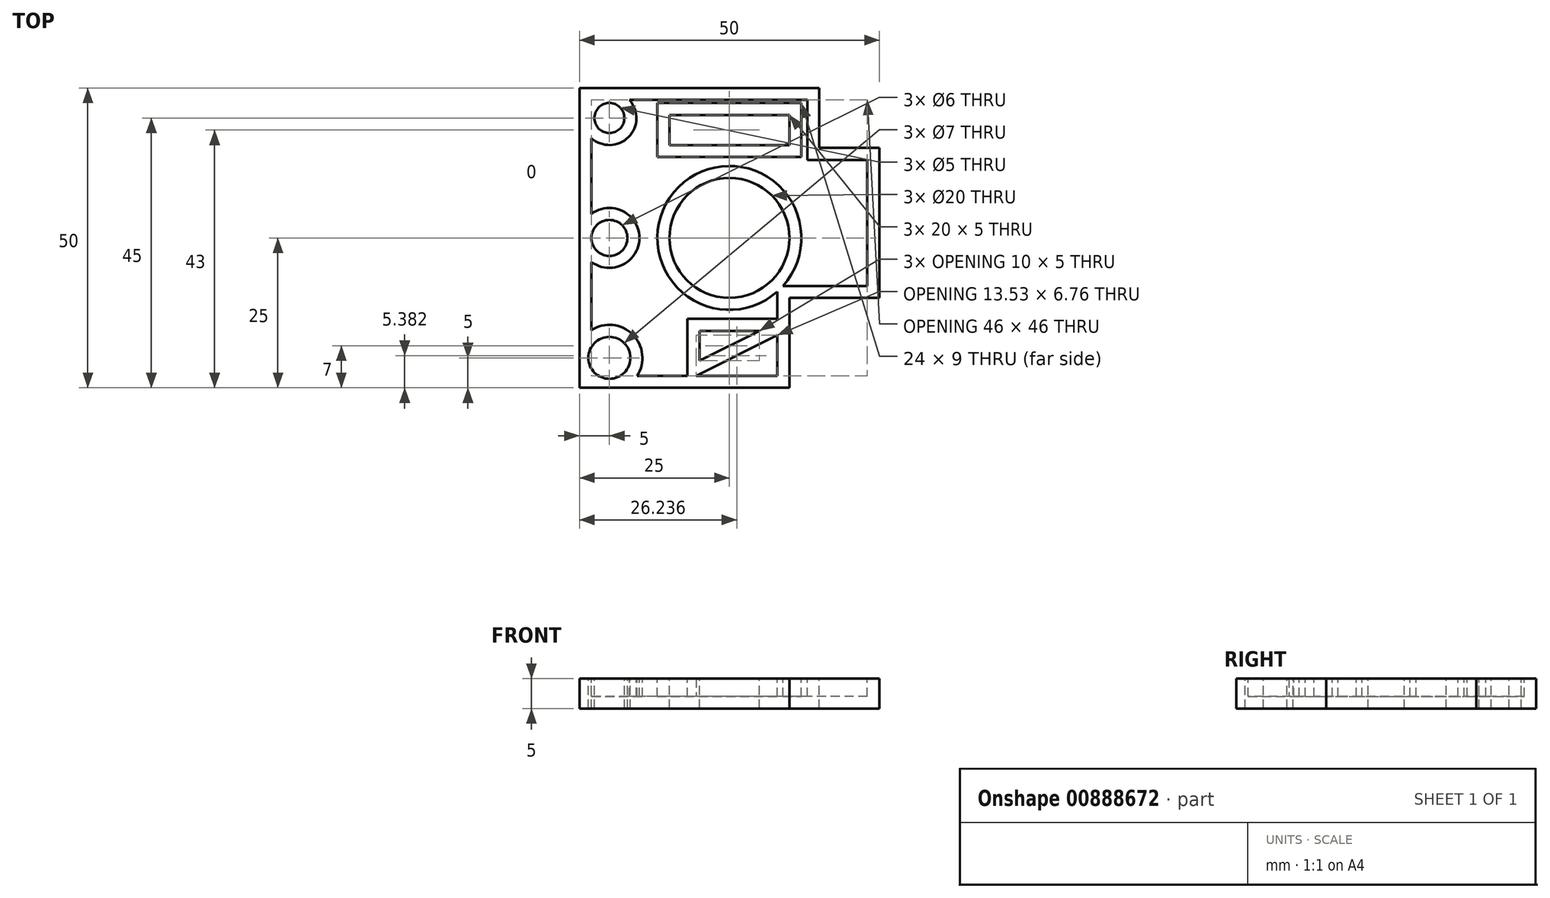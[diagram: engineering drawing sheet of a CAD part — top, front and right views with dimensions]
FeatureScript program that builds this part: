
annotation { "Feature Type Name" : "Feature", "Feature Type Description" : "" }
export const myFeature = defineFeature(function(context is Context, id is Id, definition is map)
    precondition{}
    {
        {
            var Q0;
            Q0=qCreatedBy(makeId("Top.planeOp"),FACE);
            var sketch = newSketch(context, id + "F0", { "sketchPlane" : qUnion([Q0])});
            skLineSegment(sketch, "E0.bottom", {"start": v(25, -25) * mm, "end": v(-25, -25) * mm});
            skLineSegment(sketch, "E0.top", {"start": v(25, 25) * mm, "end": v(-25, 25) * mm});
            skLineSegment(sketch, "E0.left", {"start": v(25, -25) * mm, "end": v(25, 25) * mm});
            skLineSegment(sketch, "E0.right", {"start": v(-25, -25) * mm, "end": v(-25, 25) * mm});
            skPoint(sketch, "E0.middle", {"position": v(0, 0) * mm});
            skSolve(sketch);
        }
        {
            var Q0;
            Q0 = qSketchRegion(id + "F0", true);
            extrude(context, id + "F1", {"entities" : qUnion([Q0]), "depth" : 5 * mm, "offsetDistance" : 25 * mm});
        }
        {
            var Q0;
            Q0=makeQuery(id+"F1.opExtrude","CAP_FACE",FACE,{"disambiguationData":[OSD([sQuery(id+"F0.wireOp",EDGE,"E0.bottom"),sQuery(id+"F0.wireOp",EDGE,"E0.top"),sQuery(id+"F0.wireOp",EDGE,"E0.left"),sQuery(id+"F0.wireOp",EDGE,"E0.right")])],"isStart":false});
            var sketch = newSketch(context, id + "F2", { "sketchPlane" : qUnion([Q0])});
            skLineSegment(sketch, "E1", {"start": v(-20, 25) * mm, "end": v(-20, -25) * mm});
            skLineSegment(sketch, "E2", {"start": v(-25, 20) * mm, "end": v(25, 20) * mm});
            skCircle(sketch, "E3", {"center": v(-20, 20) * mm, "radius": 2.5 * mm});
            skPoint(sketch, "E4", {"position": v(-20, 0) * mm});
            skCircle(sketch, "E5", {"center": v(-20, 0) * mm, "radius": 3 * mm});
            skLineSegment(sketch, "E6", {"start": v(-25, -20) * mm, "end": v(25, -20) * mm});
            skCircle(sketch, "E7", {"center": v(-20, -20) * mm, "radius": 3.5 * mm});
            skSolve(sketch);
        }
        {
            var Q0;
            Q0 = qSketchRegion(id + "F2", true);
            extrude(context, id + "F3", {"entities" : qUnion([Q0]), "operationType" : NewBodyOperationType.REMOVE, "endBound" : BoundingType.THROUGH_ALL, "oppositeDirection" : true, "depth" : 25 * mm, "offsetDistance" : 25 * mm});
        }
        {
            var Q0;
            Q0=makeQuery(id+"F1.opExtrude","CAP_FACE",FACE,{"disambiguationData":[OSD([sQuery(id+"F0.wireOp",EDGE,"E0.bottom"),sQuery(id+"F0.wireOp",EDGE,"E0.top"),sQuery(id+"F0.wireOp",EDGE,"E0.left"),sQuery(id+"F0.wireOp",EDGE,"E0.right")])],"isStart":false});
            var sketch = newSketch(context, id + "F4", { "sketchPlane" : qUnion([Q0])});
            skCircle(sketch, "E8", {"center": v(0, 0) * mm, "radius": 10 * mm});
            skSolve(sketch);
        }
        {
            var Q0;
            Q0 = qSketchRegion(id + "F4", true);
            extrude(context, id + "F5", {"entities" : qUnion([Q0]), "operationType" : NewBodyOperationType.REMOVE, "endBound" : BoundingType.THROUGH_ALL, "oppositeDirection" : true, "depth" : 25 * mm, "offsetDistance" : 25 * mm});
        }
        {
            var Q0;
            Q0=makeQuery(id+"F1.opExtrude","CAP_FACE",FACE,{"disambiguationData":[OSD([sQuery(id+"F0.wireOp",EDGE,"E0.bottom"),sQuery(id+"F0.wireOp",EDGE,"E0.top"),sQuery(id+"F0.wireOp",EDGE,"E0.left"),sQuery(id+"F0.wireOp",EDGE,"E0.right")])],"isStart":false});
            var sketch = newSketch(context, id + "F6", { "sketchPlane" : qUnion([Q0])});
            skLineSegment(sketch, "E9.bottom", {"start": v(25, 25) * mm, "end": v(15, 25) * mm});
            skLineSegment(sketch, "E9.top", {"start": v(25, 15) * mm, "end": v(15, 15) * mm});
            skLineSegment(sketch, "E9.left", {"start": v(25, 25) * mm, "end": v(25, 15) * mm});
            skLineSegment(sketch, "E9.right", {"start": v(15, 25) * mm, "end": v(15, 15) * mm});
            skSolve(sketch);
        }
        {
            var Q0;
            Q0 = qSketchRegion(id + "F6", true);
            extrude(context, id + "F7", {"entities" : qUnion([Q0]), "operationType" : NewBodyOperationType.REMOVE, "endBound" : BoundingType.THROUGH_ALL, "oppositeDirection" : true, "depth" : 25 * mm, "offsetDistance" : 25 * mm});
        }
        {
            var Q0;
            Q0=makeQuery(id+"F1.opExtrude","CAP_FACE",FACE,{"disambiguationData":[OSD([sQuery(id+"F0.wireOp",EDGE,"E0.bottom"),sQuery(id+"F0.wireOp",EDGE,"E0.top"),sQuery(id+"F0.wireOp",EDGE,"E0.left"),sQuery(id+"F0.wireOp",EDGE,"E0.right")])],"isStart":false});
            var sketch = newSketch(context, id + "F8", { "sketchPlane" : qUnion([Q0])});
            skLineSegment(sketch, "E10.bottom", {"start": v(25, -25) * mm, "end": v(10, -25) * mm});
            skLineSegment(sketch, "E10.top", {"start": v(25, -10) * mm, "end": v(10, -10) * mm});
            skLineSegment(sketch, "E10.left", {"start": v(25, -25) * mm, "end": v(25, -10) * mm});
            skLineSegment(sketch, "E10.right", {"start": v(10, -25) * mm, "end": v(10, -10) * mm});
            skSolve(sketch);
        }
        {
            var Q0;
            Q0 = qSketchRegion(id + "F8", true);
            extrude(context, id + "F9", {"entities" : qUnion([Q0]), "operationType" : NewBodyOperationType.REMOVE, "endBound" : BoundingType.THROUGH_ALL, "oppositeDirection" : true, "depth" : 25 * mm, "offsetDistance" : 25 * mm});
        }
        {
            var Q0;
            Q0=makeQuery(id+"F1.opExtrude","CAP_FACE",FACE,{"disambiguationData":[OSD([sQuery(id+"F0.wireOp",EDGE,"E0.bottom"),sQuery(id+"F0.wireOp",EDGE,"E0.top"),sQuery(id+"F0.wireOp",EDGE,"E0.left"),sQuery(id+"F0.wireOp",EDGE,"E0.right")])],"isStart":false});
            var sketch = newSketch(context, id + "F10", { "sketchPlane" : qUnion([Q0])});
            skPoint(sketch, "E11", {"position": v(0, 18) * mm});
            skLineSegment(sketch, "E12.bottom", {"start": v(10, 15.5) * mm, "end": v(-10, 15.5) * mm});
            skLineSegment(sketch, "E12.top", {"start": v(10, 20.5) * mm, "end": v(-10, 20.5) * mm});
            skLineSegment(sketch, "E12.left", {"start": v(10, 15.5) * mm, "end": v(10, 20.5) * mm});
            skLineSegment(sketch, "E12.right", {"start": v(-10, 15.5) * mm, "end": v(-10, 20.5) * mm});
            skSolve(sketch);
        }
        {
            var Q0;
            Q0 = qSketchRegion(id + "F10", true);
            extrude(context, id + "F11", {"entities" : qUnion([Q0]), "operationType" : NewBodyOperationType.REMOVE, "endBound" : BoundingType.THROUGH_ALL, "oppositeDirection" : true, "depth" : 25 * mm, "offsetDistance" : 25 * mm});
        }
        {
            var Q0;
            Q0=makeQuery(id+"F1.opExtrude","CAP_FACE",FACE,{"disambiguationData":[OSD([sQuery(id+"F0.wireOp",EDGE,"E0.bottom"),sQuery(id+"F0.wireOp",EDGE,"E0.top"),sQuery(id+"F0.wireOp",EDGE,"E0.left"),sQuery(id+"F0.wireOp",EDGE,"E0.right")])],"isStart":false});
            var sketch = newSketch(context, id + "F12", { "sketchPlane" : qUnion([Q0])});
            skPoint(sketch, "E13", {"position": v(0, -18) * mm});
            skLineSegment(sketch, "E14.bottom", {"start": v(5, -15.5) * mm, "end": v(-5, -15.5) * mm});
            skLineSegment(sketch, "E14.top", {"start": v(5, -20.5) * mm, "end": v(-5, -20.5) * mm});
            skLineSegment(sketch, "E14.left", {"start": v(5, -15.5) * mm, "end": v(5, -20.5) * mm});
            skLineSegment(sketch, "E14.right", {"start": v(-5, -15.5) * mm, "end": v(-5, -20.5) * mm});
            skLineSegment(sketch, "E15", {"start": v(5, -15.5) * mm, "end": v(-5, -20.5) * mm});
            skSolve(sketch);
        }
        {
            var Q0;
            Q0=makeQuery(id+"F12.imprint","IMPRINT",FACE,{"disambiguationData":[TD([[makeQuery(id+"F12.imprint","IMPRINT",EDGE,{"derivedFrom":sQuery(id+"F12.wireOp",EDGE,"E14.bottom")}),1.0]])]});
            extrude(context, id + "F13", {"entities" : qUnion([Q0]), "operationType" : NewBodyOperationType.REMOVE, "endBound" : BoundingType.THROUGH_ALL, "oppositeDirection" : true, "depth" : 25 * mm, "offsetDistance" : 25 * mm});
        }
        {
            var Q0;
            Q0=makeQuery(id+"F1.opExtrude","CAP_FACE",FACE,{"disambiguationData":[OSD([sQuery(id+"F0.wireOp",EDGE,"E0.bottom"),sQuery(id+"F0.wireOp",EDGE,"E0.top"),sQuery(id+"F0.wireOp",EDGE,"E0.left"),sQuery(id+"F0.wireOp",EDGE,"E0.right")])],"isStart":false});
            shell(context, id + "F14", {"entities" : qUnion([Q0]), "thickness" : 2 * mm});
        }
    });
